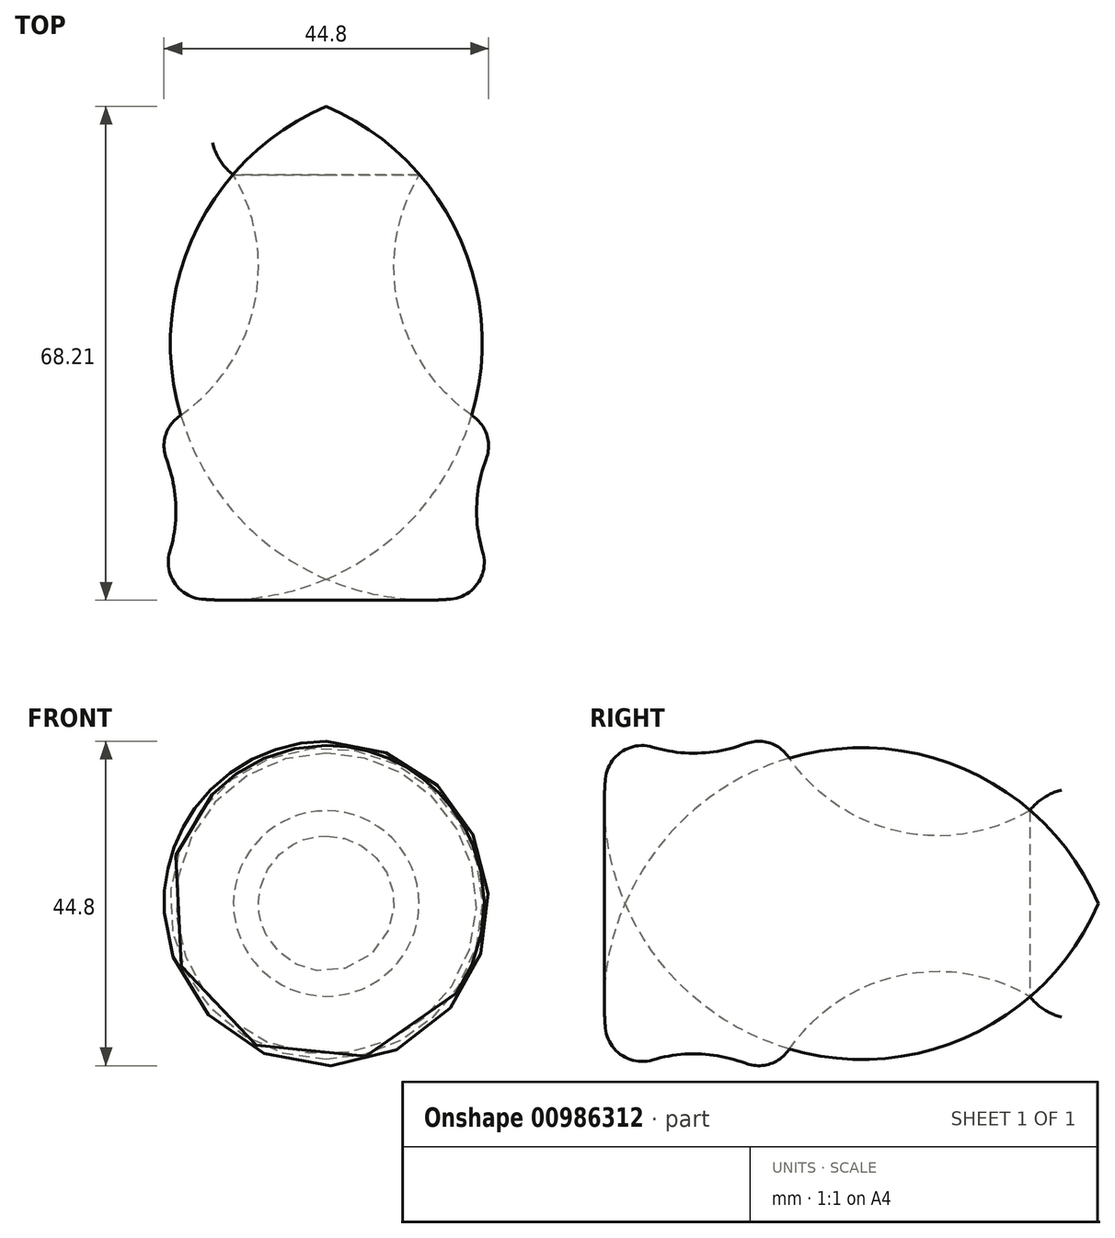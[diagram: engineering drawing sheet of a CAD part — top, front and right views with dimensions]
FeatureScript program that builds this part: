
annotation { "Feature Type Name" : "Feature", "Feature Type Description" : "" }
export const myFeature = defineFeature(function(context is Context, id is Id, definition is map)
    precondition{}
    {
        {
            var Q0;
            Q0=qCreatedBy(makeId("Top.planeOp"),FACE);
            var sketch = newSketch(context, id + "F0", { "sketchPlane" : qUnion([Q0])});
            skArc(sketch, "E0", {"start": v(0, -29.79) * mm, "mid": v(11.9, -32.6) * mm, "end": v(24.03, -31.23) * mm});
            skArc(sketch, "E1", {"start": v(24.03, -9.35) * mm, "mid": v(20.76, -20.3) * mm, "end": v(24.03, -31.23) * mm});
            skArc(sketch, "E2", {"start": v(12.8, 26.05) * mm, "mid": v(10.52, 5.84) * mm, "end": v(24.03, -9.35) * mm});
            skArc(sketch, "E3", {"start": v(12.8, 26.05) * mm, "mid": v(12.27, 39.22) * mm, "end": v(0, 34.4) * mm});
            skLineSegment(sketch, "E4", {"start": v(0, 34.4) * mm, "end": v(0, -29.79) * mm});
            skSolve(sketch);
        }
        {
            var Q0;
            Q0 = qSketchRegion(id + "F0", true);
            var Q1;
            Q1=sQuery(id+"F0.wireOp",EDGE,"E4");
            revolve(context, id + "F1", {"surfaceOperationType" : NewSurfaceOperationType.NEW, "entities" : qUnion([Q0]), "axis" : qUnion([Q1]), "revolveType" : RevolveType.FULL});
        }
        {
            var Q0;
            Q0=makeQuery(id+"F1.opRevolve","SWEPT_FACE",FACE,{"disambiguationData":[OSD([sQuery(id+"F0.wireOp",EDGE,"E1")])]});
            fillet(context, id + "F2", {"entities" : qUnion([Q0]), "radius" : 5.08 * mm, "tangentPropagation" : true, "allowEdgeOverflow" : false});
        }
    });
